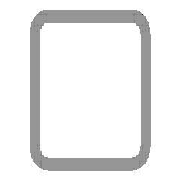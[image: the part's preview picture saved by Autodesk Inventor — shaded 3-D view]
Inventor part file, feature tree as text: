
AUTODESK INVENTOR PART (.ipt)
format: ipt  version: 2025.1 (Build 291241020, 241B)  size: 142,848 bytes
history: native  units: mm (DEFAULTED — no unit token found)
features: other x4, sketch x1, plane x1
ambient origin geometry x8: Origin, YZ Plane, XZ Plane, XY Plane, X Axis, Y Axis, Z Axis, Center Point
bodies: Solid1 (feature_tree), Body (feature_tree)
feature tree (6):
  parser-record x1  (decoder bookkeeping rows leaked as tree rows — omitted from the tree; the rows remain in map.json)
  other  "Driven Length"
  other  "Start Plane"
  other  "End Plane"
  sketch  "Sketch3"  dims[d3=550.0mm d4=0.0mm d7=8.0mm d9=100.0mm d11=100.0mm d12=4.0mm d13=100.0mm d14=650.0mm d15=50.0mm d16=50.0mm d17=90.0deg d18=550.0mm]
  plane  "Work Plane3"
